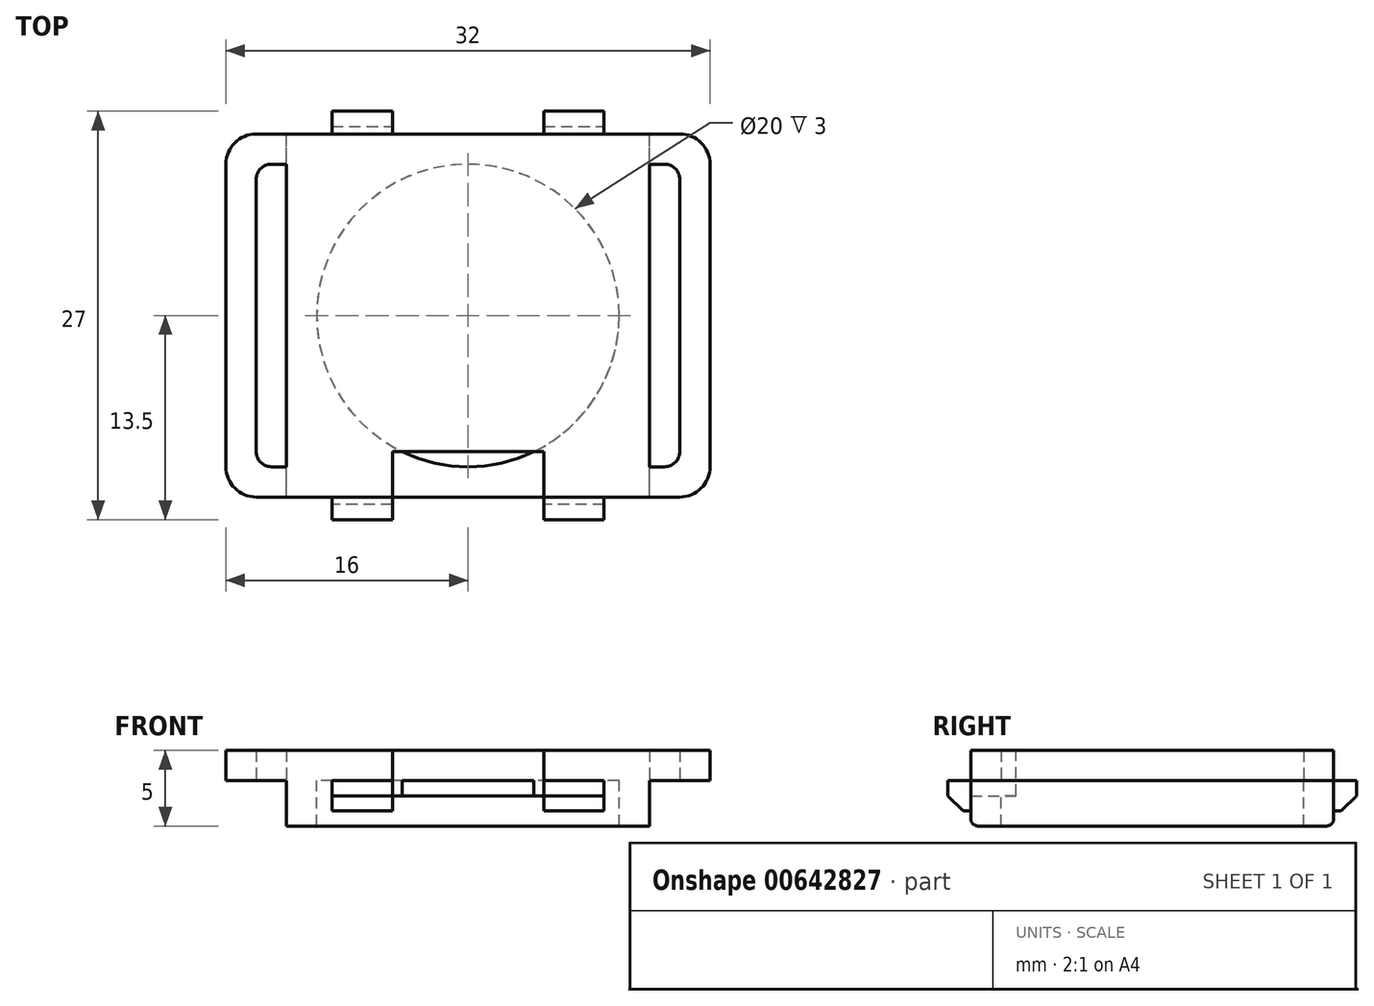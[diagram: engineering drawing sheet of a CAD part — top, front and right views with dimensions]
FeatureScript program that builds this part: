
annotation { "Feature Type Name" : "Feature", "Feature Type Description" : "" }
export const myFeature = defineFeature(function(context is Context, id is Id, definition is map)
    precondition{}
    {
        {
            var Q0;
            Q0=qCreatedBy(makeId("Top.planeOp"),FACE);
            var sketch = newSketch(context, id + "F0", { "sketchPlane" : qUnion([Q0])});
            skLineSegment(sketch, "E0.bottom", {"start": v(12, -12) * mm, "end": v(-12, -12) * mm});
            skLineSegment(sketch, "E0.top", {"start": v(12, 12) * mm, "end": v(-12, 12) * mm});
            skLineSegment(sketch, "E0.left", {"start": v(12, -12) * mm, "end": v(12, 12) * mm});
            skLineSegment(sketch, "E0.right", {"start": v(-12, -12) * mm, "end": v(-12, 12) * mm});
            skPoint(sketch, "E0.middle", {"position": v(0, 0) * mm});
            skSolve(sketch);
        }
        {
            var Q0;
            Q0=qCreatedBy(makeId("Top.planeOp"),FACE);
            var sketch = newSketch(context, id + "F1", { "sketchPlane" : qUnion([Q0])});
            skCircle(sketch, "E1", {"center": v(0, 0) * mm, "radius": 10 * mm});
            skSolve(sketch);
        }
        {
            var Q0;
            Q0=qCreatedBy(makeId("Top.planeOp"),FACE);
            var sketch = newSketch(context, id + "F2", { "sketchPlane" : qUnion([Q0])});
            skLineSegment(sketch, "E2.bottom", {"start": v(16, -12) * mm, "end": v(-16, -12) * mm});
            skLineSegment(sketch, "E2.top", {"start": v(16, 12) * mm, "end": v(-16, 12) * mm});
            skLineSegment(sketch, "E2.left", {"start": v(16, -12) * mm, "end": v(16, 12) * mm});
            skLineSegment(sketch, "E2.right", {"start": v(-16, -12) * mm, "end": v(-16, 12) * mm});
            skPoint(sketch, "E2.middle", {"position": v(0, 0) * mm});
            skSolve(sketch);
        }
        {
            var Q0;
            Q0 = qSketchRegion(id + "F2", true);
            extrude(context, id + "F3", {"entities" : qUnion([Q0]), "depth" : 2 * mm, "offsetDistance" : 25 * mm});
        }
        {
            var Q0;
            Q0 = qSketchRegion(id + "F0", true);
            extrude(context, id + "F4", {"entities" : qUnion([Q0]), "operationType" : NewBodyOperationType.ADD, "oppositeDirection" : true, "depth" : 3 * mm, "offsetDistance" : 25 * mm});
        }
        {
            var Q0;
            Q0 = qSketchRegion(id + "F1", true);
            extrude(context, id + "F5", {"entities" : qUnion([Q0]), "operationType" : NewBodyOperationType.REMOVE, "oppositeDirection" : true, "depth" : 3 * mm, "offsetDistance" : 25 * mm});
        }
        {
            var Q0;
            Q0=qCreatedBy(makeId("Top.planeOp"),FACE);
            var sketch = newSketch(context, id + "F6", { "sketchPlane" : qUnion([Q0])});
            skLineSegment(sketch, "E3.bottom", {"start": v(-12, -10) * mm, "end": v(-14, -10) * mm});
            skLineSegment(sketch, "E3.top", {"start": v(-12, 10) * mm, "end": v(-14, 10) * mm});
            skLineSegment(sketch, "E3.left", {"start": v(-12, -10) * mm, "end": v(-12, 10) * mm});
            skLineSegment(sketch, "E3.right", {"start": v(-14, -10) * mm, "end": v(-14, 10) * mm});
            skPoint(sketch, "E3.middle", {"position": v(-13, 0) * mm});
            skLineSegment(sketch, "E4.bottom", {"start": v(14, -10) * mm, "end": v(12, -10) * mm});
            skLineSegment(sketch, "E4.top", {"start": v(14, 10) * mm, "end": v(12, 10) * mm});
            skLineSegment(sketch, "E4.left", {"start": v(14, -10) * mm, "end": v(14, 10) * mm});
            skLineSegment(sketch, "E4.right", {"start": v(12, -10) * mm, "end": v(12, 10) * mm});
            skPoint(sketch, "E4.middle", {"position": v(13, 0) * mm});
            skSolve(sketch);
        }
        {
            var Q0;
            Q0 = qSketchRegion(id + "F6", true);
            extrude(context, id + "F7", {"entities" : qUnion([Q0]), "operationType" : NewBodyOperationType.REMOVE, "depth" : 2 * mm, "offsetDistance" : 25 * mm});
        }
        {
            var Q0;
            Q0=makeQuery(id+"F3.opExtrude","SWEPT_EDGE",EDGE,{"disambiguationData":[OSD([sQuery(id+"F2.wireOp",EDGE,"E2.bottom"),sQuery(id+"F2.wireOp",EDGE,"E2.left")])]});
            var Q1;
            Q1=makeQuery(id+"F3.opExtrude","SWEPT_EDGE",EDGE,{"disambiguationData":[OSD([sQuery(id+"F2.wireOp",EDGE,"E2.top"),sQuery(id+"F2.wireOp",EDGE,"E2.left")])]});
            var Q2;
            Q2=makeQuery(id+"F3.opExtrude","SWEPT_EDGE",EDGE,{"disambiguationData":[OSD([sQuery(id+"F2.wireOp",EDGE,"E2.bottom"),sQuery(id+"F2.wireOp",EDGE,"E2.right")])]});
            var Q3;
            Q3=makeQuery(id+"F3.opExtrude","SWEPT_EDGE",EDGE,{"disambiguationData":[OSD([sQuery(id+"F2.wireOp",EDGE,"E2.top"),sQuery(id+"F2.wireOp",EDGE,"E2.right")])]});
            fillet(context, id + "F8", {"entities" : qUnion([Q0, Q1, Q2, Q3]), "radius" : 2 * mm, "tangentPropagation" : true, "allowEdgeOverflow" : false});
        }
        {
            var Q0;
            Q0=makeQuery(id+"F7.boolean.opBoolean","COPY",EDGE,{"derivedFrom":makeQuery(id+"F7.opExtrude","SWEPT_EDGE",EDGE,{"disambiguationData":[OSD([sQuery(id+"F6.wireOp",EDGE,"E3.top"),sQuery(id+"F6.wireOp",EDGE,"E3.right")])]})});
            var Q1;
            Q1=makeQuery(id+"F7.boolean.opBoolean","COPY",EDGE,{"derivedFrom":makeQuery(id+"F7.opExtrude","SWEPT_EDGE",EDGE,{"disambiguationData":[OSD([sQuery(id+"F6.wireOp",EDGE,"E4.top"),sQuery(id+"F6.wireOp",EDGE,"E4.left")])]})});
            var Q2;
            Q2=makeQuery(id+"F7.boolean.opBoolean","COPY",EDGE,{"derivedFrom":makeQuery(id+"F7.opExtrude","SWEPT_EDGE",EDGE,{"disambiguationData":[OSD([sQuery(id+"F6.wireOp",EDGE,"E3.bottom"),sQuery(id+"F6.wireOp",EDGE,"E3.right")])]})});
            var Q3;
            Q3=makeQuery(id+"F7.boolean.opBoolean","COPY",EDGE,{"derivedFrom":makeQuery(id+"F7.opExtrude","SWEPT_EDGE",EDGE,{"disambiguationData":[OSD([sQuery(id+"F6.wireOp",EDGE,"E4.bottom"),sQuery(id+"F6.wireOp",EDGE,"E4.left")])]})});
            fillet(context, id + "F9", {"entities" : qUnion([Q0, Q1, Q2, Q3]), "radius" : 1 * mm, "tangentPropagation" : true, "allowEdgeOverflow" : false});
        }
        {
            var Q0;
            Q0=qCreatedBy(makeId("Top.planeOp"),FACE);
            var sketch = newSketch(context, id + "F10", { "sketchPlane" : qUnion([Q0])});
            skLineSegment(sketch, "E5.bottom", {"start": v(5, -12) * mm, "end": v(-5, -12) * mm});
            skLineSegment(sketch, "E5.top", {"start": v(5, -9) * mm, "end": v(-5, -9) * mm});
            skLineSegment(sketch, "E5.left", {"start": v(5, -12) * mm, "end": v(5, -9) * mm});
            skLineSegment(sketch, "E5.right", {"start": v(-5, -12) * mm, "end": v(-5, -9) * mm});
            skPoint(sketch, "E5.middle", {"position": v(0, -10.5) * mm});
            skSolve(sketch);
        }
        {
            var Q0;
            Q0 = qSketchRegion(id + "F10", true);
            extrude(context, id + "F11", {"entities" : qUnion([Q0]), "operationType" : NewBodyOperationType.REMOVE, "oppositeDirection" : true, "depth" : 1 * mm, "offsetDistance" : 25 * mm});
        }
        {
            var Q0;
            Q0 = qSketchRegion(id + "F10", true);
            extrude(context, id + "F12", {"entities" : qUnion([Q0]), "operationType" : NewBodyOperationType.REMOVE, "depth" : 2 * mm, "offsetDistance" : 25 * mm});
        }
        {
            var Q0;
            Q0=qCreatedBy(makeId("Top.planeOp"),FACE);
            var sketch = newSketch(context, id + "F13", { "sketchPlane" : qUnion([Q0])});
            skLineSegment(sketch, "E6.bottom", {"start": v(-5, -12) * mm, "end": v(-9, -12) * mm});
            skLineSegment(sketch, "E6.top", {"start": v(-5, -13.5) * mm, "end": v(-9, -13.5) * mm});
            skLineSegment(sketch, "E6.left", {"start": v(-5, -12) * mm, "end": v(-5, -13.5) * mm});
            skLineSegment(sketch, "E6.right", {"start": v(-9, -12) * mm, "end": v(-9, -13.5) * mm});
            skLineSegment(sketch, "E7.0.1.0", {"start": v(-5, 13.5) * mm, "end": v(-9, 13.5) * mm});
            skLineSegment(sketch, "E7.0.1.1", {"start": v(-5, 12) * mm, "end": v(-9, 12) * mm});
            skLineSegment(sketch, "E7.0.1.2", {"start": v(-5, 13.5) * mm, "end": v(-5, 12) * mm});
            skLineSegment(sketch, "E7.0.1.3", {"start": v(-9, 13.5) * mm, "end": v(-9, 12) * mm});
            skLineSegment(sketch, "E7.1.0.0", {"start": v(9, -12) * mm, "end": v(5, -12) * mm});
            skLineSegment(sketch, "E7.1.0.1", {"start": v(9, -13.5) * mm, "end": v(5, -13.5) * mm});
            skLineSegment(sketch, "E7.1.0.2", {"start": v(9, -12) * mm, "end": v(9, -13.5) * mm});
            skLineSegment(sketch, "E7.1.0.3", {"start": v(5, -12) * mm, "end": v(5, -13.5) * mm});
            skLineSegment(sketch, "E7.1.1.0", {"start": v(9, 13.5) * mm, "end": v(5, 13.5) * mm});
            skLineSegment(sketch, "E7.1.1.1", {"start": v(9, 12) * mm, "end": v(5, 12) * mm});
            skLineSegment(sketch, "E7.1.1.2", {"start": v(9, 13.5) * mm, "end": v(9, 12) * mm});
            skLineSegment(sketch, "E7.1.1.3", {"start": v(5, 13.5) * mm, "end": v(5, 12) * mm});
            skLineSegment(sketch, "E7.direction1", {"start": v(-9, -13.5) * mm, "end": v(5, -13.5) * mm, "construction": true});
            skLineSegment(sketch, "E7.direction2", {"start": v(-9, -13.5) * mm, "end": v(-9, 12) * mm, "construction": true});
            skSolve(sketch);
        }
        {
            var Q0;
            Q0 = qSketchRegion(id + "F13", true);
            extrude(context, id + "F14", {"entities" : qUnion([Q0]), "operationType" : NewBodyOperationType.ADD, "oppositeDirection" : true, "depth" : 2 * mm, "offsetDistance" : 25 * mm});
        }
        {
            var Q0;
            Q0=makeQuery(id+"F14.opExtrude","CAP_EDGE",EDGE,{"disambiguationData":[OSD([sQuery(id+"F13.wireOp",EDGE,"E6.top")])],"isStart":false});
            var Q1;
            Q1=makeQuery(id+"F14.opExtrude","CAP_EDGE",EDGE,{"disambiguationData":[OSD([sQuery(id+"F13.wireOp",EDGE,"E7.1.0.1")])],"isStart":false});
            var Q2;
            Q2=makeQuery(id+"F14.opExtrude","CAP_EDGE",EDGE,{"disambiguationData":[OSD([sQuery(id+"F13.wireOp",EDGE,"E7.1.1.0")])],"isStart":false});
            var Q3;
            Q3=makeQuery(id+"F14.opExtrude","CAP_EDGE",EDGE,{"disambiguationData":[OSD([sQuery(id+"F13.wireOp",EDGE,"E7.0.1.0")])],"isStart":false});
            chamfer(context, id + "F15", {"entities" : qUnion([Q0, Q1, Q2, Q3]), "width" : 1 * mm, "tangentPropagation" : true});
        }
        {
            var Q0;
            Q0=makeQuery(id+"F4.opExtrude","CAP_EDGE",EDGE,{"disambiguationData":[OSD([sQuery(id+"F0.wireOp",EDGE,"E0.bottom")])],"isStart":false});
            var Q1;
            Q1=makeQuery(id+"F4.opExtrude","CAP_EDGE",EDGE,{"disambiguationData":[OSD([sQuery(id+"F0.wireOp",EDGE,"E0.top")])],"isStart":false});
            fillet(context, id + "F16", {"entities" : qUnion([Q0, Q1]), "radius" : 0.5 * mm, "tangentPropagation" : true, "allowEdgeOverflow" : false});
        }
    });
